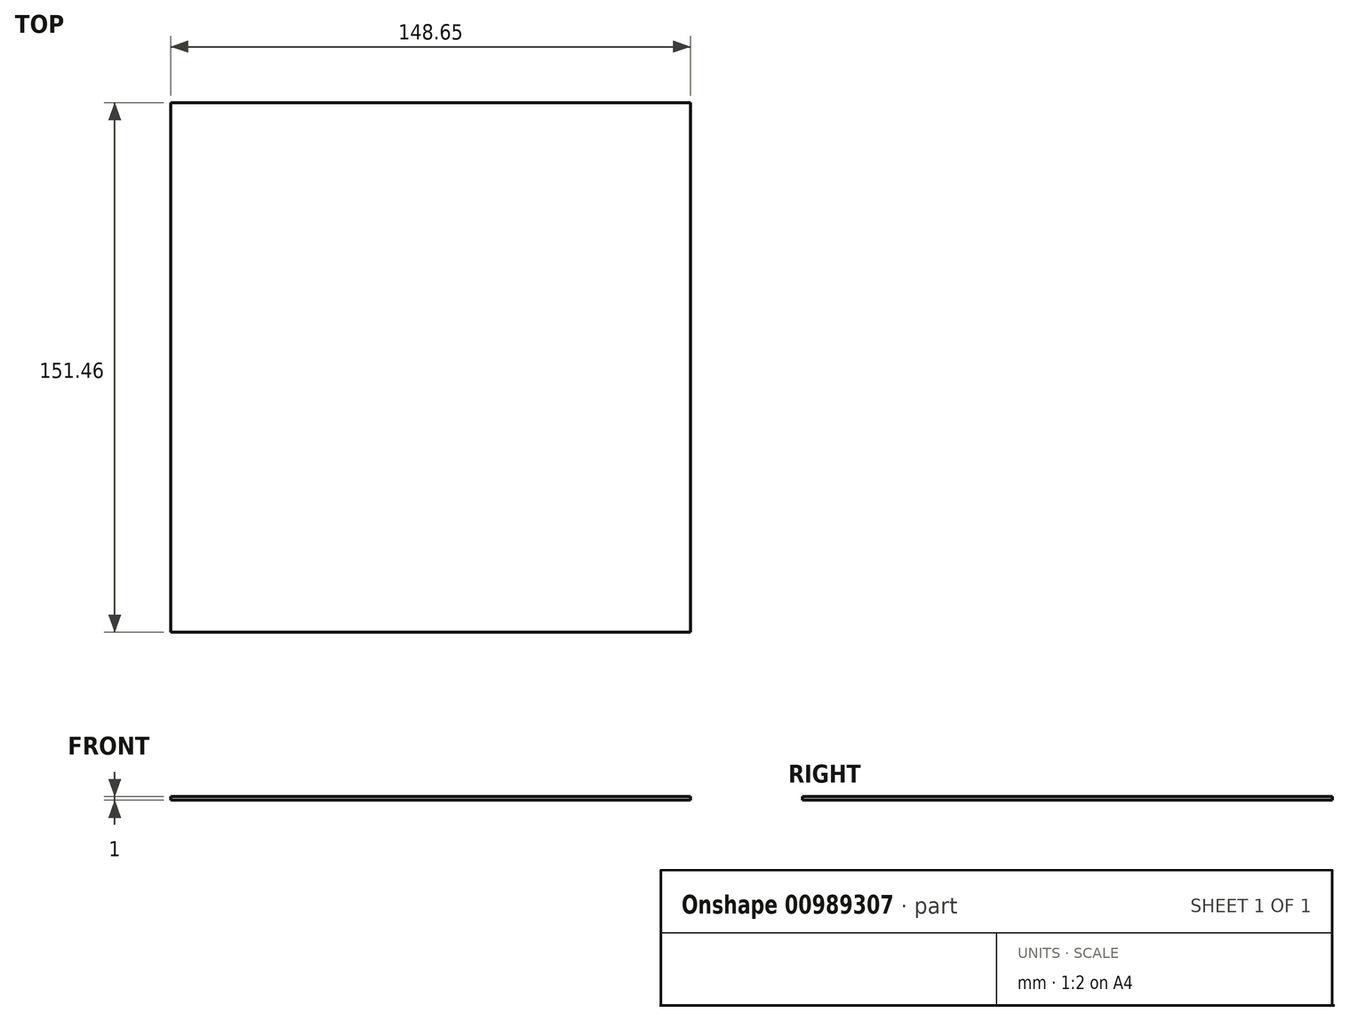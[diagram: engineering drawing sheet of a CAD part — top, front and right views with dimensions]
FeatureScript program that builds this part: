
annotation { "Feature Type Name" : "Feature", "Feature Type Description" : "" }
export const myFeature = defineFeature(function(context is Context, id is Id, definition is map)
    precondition{}
    {
        {
            var Q0;
            Q0=qCreatedBy(makeId("Top.planeOp"),FACE);
            var sketch = newSketch(context, id + "F0", { "sketchPlane" : qUnion([Q0])});
            skLineSegment(sketch, "E0.bottom", {"start": v(-74.43, 77.1) * mm, "end": v(74.22, 77.1) * mm});
            skLineSegment(sketch, "E0.top", {"start": v(-74.43, -74.36) * mm, "end": v(74.22, -74.36) * mm});
            skLineSegment(sketch, "E0.left", {"start": v(-74.43, 77.1) * mm, "end": v(-74.43, -74.36) * mm});
            skLineSegment(sketch, "E0.right", {"start": v(74.22, 77.1) * mm, "end": v(74.22, -74.36) * mm});
            skSolve(sketch);
        }
        {
            var Q0;
            Q0=makeQuery(id+"F0.imprint","IMPRINT",FACE,{"disambiguationData":[TD([[makeQuery(id+"F0.imprint","IMPRINT",EDGE,{"derivedFrom":sQuery(id+"F0.wireOp",EDGE,"E0.bottom")}),-1.0]])]});
            extrude(context, id + "F1", {"entities" : qUnion([Q0]), "depth" : 1 * mm, "offsetDistance" : 25.4 * mm});
        }
    });
